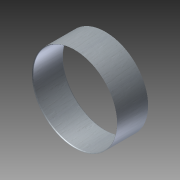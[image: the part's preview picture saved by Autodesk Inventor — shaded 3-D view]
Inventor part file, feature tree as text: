
AUTODESK INVENTOR PART (.ipt)
format: ipt  version: 2011 SP1 (Build 150282100, 282)  size: 98,304 bytes
history: native  units: in
note: dims shown in document units (in); Inventor stores cm internally (conversion verified against a paired STEP export)
features: extrude x1, fillet x1, sketch x1
ambient origin geometry x8: Origin, YZ Plane, XZ Plane, XY Plane, X Axis, Y Axis, Z Axis, Center Point
bodies: Solid1 (feature_tree)
feature tree (3):
  extrude  "Extrusion1"  Depth=8.125in
  fillet  "Fillet1"  Radius=3.0in
  sketch  "Sketch1"  dims[d0=0.0625in d1=8.125in d2=3.0in d3=0.0in d4=0.125in]
